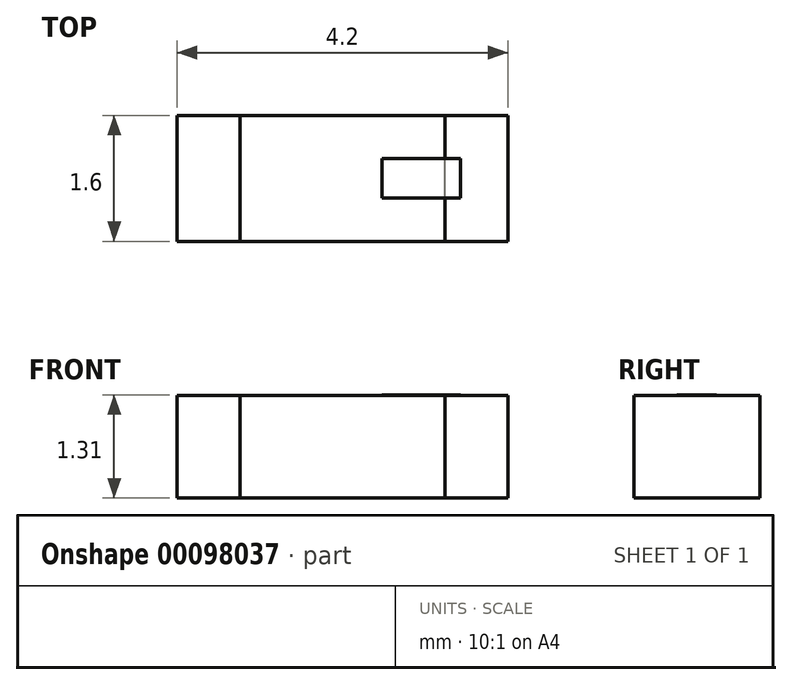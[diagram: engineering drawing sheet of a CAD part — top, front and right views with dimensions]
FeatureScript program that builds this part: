
annotation { "Feature Type Name" : "Feature", "Feature Type Description" : "" }
export const myFeature = defineFeature(function(context is Context, id is Id, definition is map)
    precondition{}
    {
        {
            var Q0;
            Q0=qCreatedBy(makeId("Top.planeOp"),FACE);
            var sketch = newSketch(context, id + "F0", { "sketchPlane" : qUnion([Q0])});
            skLineSegment(sketch, "E0.bottom", {"start": v(-2.1, 0.8) * mm, "end": v(2.1, 0.8) * mm});
            skLineSegment(sketch, "E0.top", {"start": v(-2.1, -0.8) * mm, "end": v(2.1, -0.8) * mm});
            skLineSegment(sketch, "E0.left", {"start": v(-2.1, 0.8) * mm, "end": v(-2.1, -0.8) * mm});
            skLineSegment(sketch, "E0.right", {"start": v(2.1, 0.8) * mm, "end": v(2.1, -0.8) * mm});
            skPoint(sketch, "E0.middle", {"position": v(0, 0) * mm});
            skLineSegment(sketch, "E1", {"start": v(-1.3, 0.8) * mm, "end": v(-1.3, -0.8) * mm});
            skLineSegment(sketch, "E2", {"start": v(1.3, -0.8) * mm, "end": v(1.3, 0.8) * mm});
            skSolve(sketch);
        }
        {
            var Q0;
            {var subQ0=sQuery(id+"F0.wireOp",EDGE,"E0.right");Q0=makeQuery(id+"F0.imprint","IMPRINT",FACE,{"disambiguationData":[TD([[makeQuery(id+"F0.imprint","IMPRINT",EDGE,{"derivedFrom":subQ0}),-1.0]])]});}
            extrude(context, id + "F1", {"entities" : qUnion([Q0]), "depth" : 1.3 * mm});
        }
        {
            var Q0;
            {var subQ0=sQuery(id+"F0.wireOp",EDGE,"E0.left");Q0=makeQuery(id+"F0.imprint","IMPRINT",FACE,{"disambiguationData":[TD([[makeQuery(id+"F0.imprint","IMPRINT",EDGE,{"derivedFrom":subQ0}),1.0]])]});}
            extrude(context, id + "F2", {"entities" : qUnion([Q0]), "depth" : 1.3 * mm});
        }
        {
            var Q0;
            {var subQ0=sQuery(id+"F0.wireOp",EDGE,"E1");Q0=makeQuery(id+"F0.imprint","IMPRINT",FACE,{"disambiguationData":[TD([[makeQuery(id+"F0.imprint","IMPRINT",EDGE,{"derivedFrom":subQ0}),1.0]])]});}
            extrude(context, id + "F3", {"entities" : qUnion([Q0]), "depth" : 1.3 * mm});
        }
        {
            var Q0;
            Q0=makeQuery(id+"F3.opExtrude","CAP_FACE",FACE,{"disambiguationData":[OSD([sQuery(id+"F0.wireOp",EDGE,"E0.bottom"),sQuery(id+"F0.wireOp",EDGE,"E0.top"),sQuery(id+"F0.wireOp",EDGE,"E1"),sQuery(id+"F0.wireOp",EDGE,"E2")])],"isStart":false});
            var sketch = newSketch(context, id + "F4", { "sketchPlane" : qUnion([Q0])});
            skLineSegment(sketch, "E3.bottom", {"start": v(1.5, -0.25) * mm, "end": v(-1.5, -0.25) * mm});
            skLineSegment(sketch, "E3.top", {"start": v(1.5, 0.25) * mm, "end": v(-1.5, 0.25) * mm});
            skLineSegment(sketch, "E3.left", {"start": v(1.5, -0.25) * mm, "end": v(1.5, 0.25) * mm});
            skLineSegment(sketch, "E3.right", {"start": v(-1.5, -0.25) * mm, "end": v(-1.5, 0.25) * mm});
            skPoint(sketch, "E3.middle", {"position": v(0, 0) * mm});
            skLineSegment(sketch, "E4", {"start": v(0.5, 0.25) * mm, "end": v(0.5, -0.25) * mm});
            skSolve(sketch);
        }
        {
            var Q0;
            {var subQ0=sQuery(id+"F4.wireOp",EDGE,"E4");Q0=makeQuery(id+"F4.imprint","IMPRINT",FACE,{"disambiguationData":[TD([[makeQuery(id+"F4.imprint","IMPRINT",EDGE,{"derivedFrom":subQ0}),1.0]])]});}
            var Q1;
            {var subQ0=sQuery(id+"F4.wireOp",EDGE,"E3.left");Q1=makeQuery(id+"F4.imprint","IMPRINT",FACE,{"disambiguationData":[TD([[makeQuery(id+"F4.imprint","IMPRINT",EDGE,{"derivedFrom":subQ0}),1.0]])]});}
            extrude(context, id + "F5", {"entities" : qUnion([Q0, Q1]), "depth" : 0.01 * mm});
        }
    });
